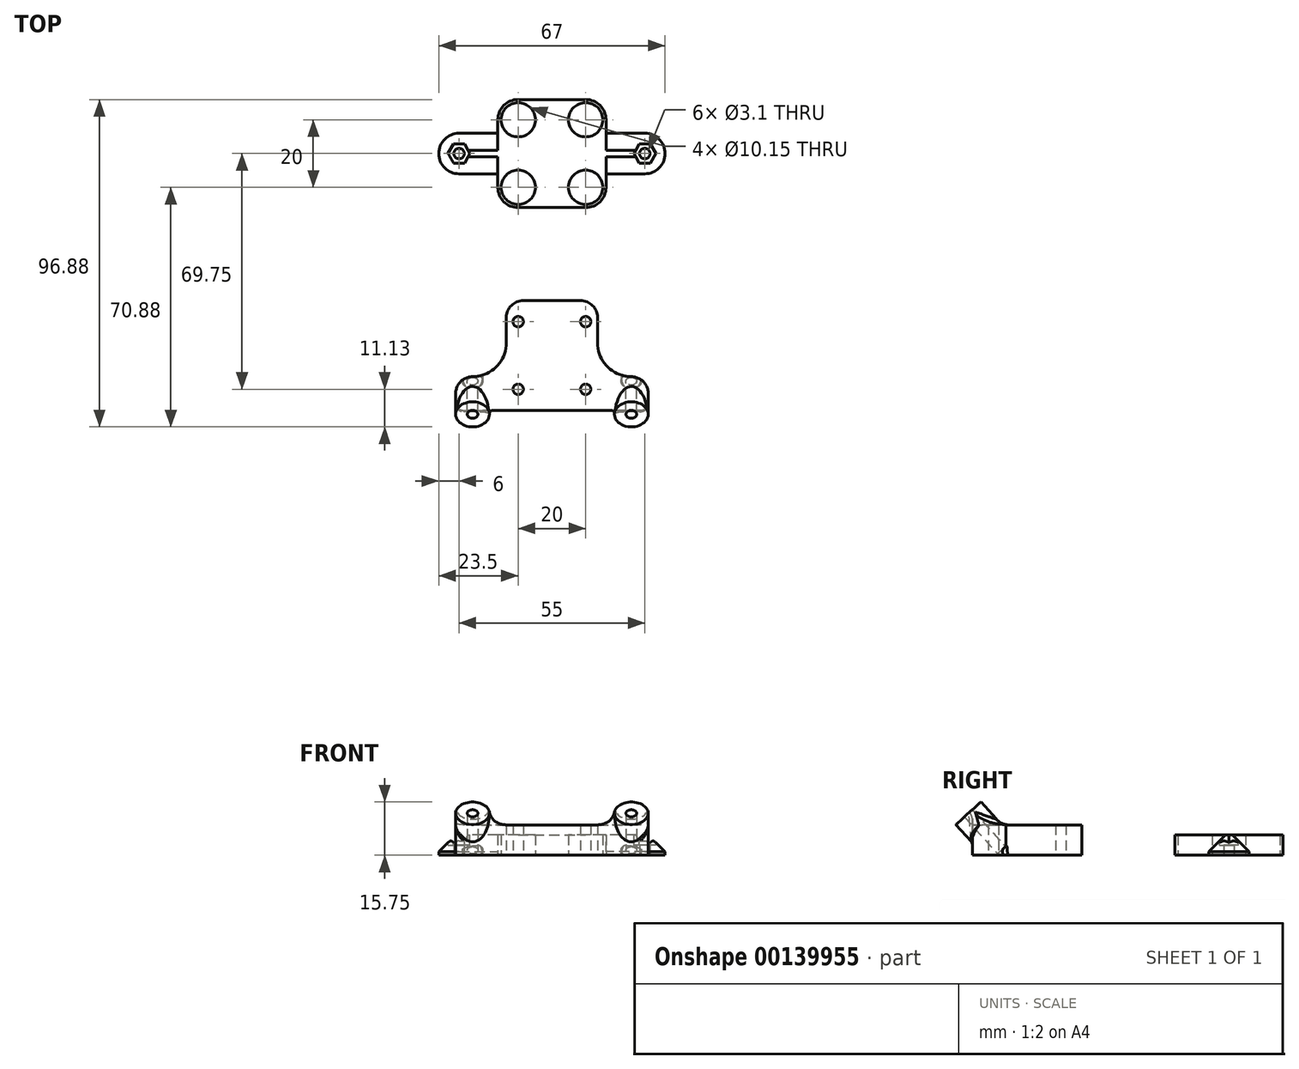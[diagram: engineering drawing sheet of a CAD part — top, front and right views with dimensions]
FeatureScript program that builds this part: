
annotation { "Feature Type Name" : "Feature", "Feature Type Description" : "" }
export const myFeature = defineFeature(function(context is Context, id is Id, definition is map)
    precondition{}
    {
        {
            var Q0;
            Q0=qCreatedBy(makeId("Top.planeOp"),FACE);
            var sketch = newSketch(context, id + "F0", { "sketchPlane" : qUnion([Q0])});
            skLineSegment(sketch, "E0.bottom", {"start": v(-13.5, 22.5) * mm, "end": v(13.5, 22.5) * mm});
            skLineSegment(sketch, "E0.top", {"start": v(-13.5, -10) * mm, "end": v(13.5, -10) * mm});
            skLineSegment(sketch, "E0.left", {"start": v(-13.5, 22.5) * mm, "end": v(-13.5, -10) * mm});
            skLineSegment(sketch, "E0.right", {"start": v(13.5, 22.5) * mm, "end": v(13.5, -10) * mm});
            skLineSegment(sketch, "E1.bottom", {"start": v(-28.5, 0) * mm, "end": v(28.5, 0) * mm});
            skLineSegment(sketch, "E1.top", {"start": v(-28.5, -10) * mm, "end": v(28.5, -10) * mm});
            skLineSegment(sketch, "E1.left", {"start": v(-28.5, 0) * mm, "end": v(-28.5, -10) * mm});
            skLineSegment(sketch, "E1.right", {"start": v(28.5, 0) * mm, "end": v(28.5, -10) * mm});
            skPoint(sketch, "E2", {"position": v(0, 0) * mm});
            skCircle(sketch, "E3", {"center": v(-10, 16.25) * mm, "radius": 1.55 * mm});
            skCircle(sketch, "E4", {"center": v(10, 16.25) * mm, "radius": 1.55 * mm});
            skCircle(sketch, "E5", {"center": v(-10, -3.75) * mm, "radius": 1.55 * mm});
            skCircle(sketch, "E6", {"center": v(10, -3.75) * mm, "radius": 1.55 * mm});
            skLineSegment(sketch, "E7", {"start": v(-10, 16.25) * mm, "end": v(-13.5, 16.25) * mm, "construction": true});
            skLineSegment(sketch, "E8", {"start": v(-10, 16.25) * mm, "end": v(-10, 22.5) * mm, "construction": true});
            skLineSegment(sketch, "E9", {"start": v(10, 16.25) * mm, "end": v(13.5, 16.25) * mm, "construction": true});
            skLineSegment(sketch, "E10", {"start": v(-10, -3.75) * mm, "end": v(-10, -10) * mm, "construction": true});
            skPoint(sketch, "E11", {"position": v(0, -10) * mm});
            skSolve(sketch);
        }
        {
            var Q0;
            {var subQ1=sQuery(id+"F0.wireOp",EDGE,"E0.bottom");Q0=makeQuery(id+"F0.imprint","IMPRINT",FACE,{"disambiguationData":[TD([[makeQuery(id+"F0.imprint","IMPRINT",EDGE,{"derivedFrom":subQ1}),-1.0]])]});}
            var Q1;
            Q1=makeQuery(id+"F0.imprint","IMPRINT",FACE,{"disambiguationData":[TD([[makeQuery(id+"F0.imprint","IMPRINT",EDGE,{"derivedFrom":sQuery(id+"F0.wireOp",EDGE,"E5")}),-1.0]])]});
            var Q2;
            {var subQ5=sQuery(id+"F0.wireOp",EDGE,"E1.right");Q2=makeQuery(id+"F0.imprint","IMPRINT",FACE,{"disambiguationData":[TD([[makeQuery(id+"F0.imprint","IMPRINT",EDGE,{"derivedFrom":subQ5}),-1.0]])]});}
            var Q3;
            {var subQ5=sQuery(id+"F0.wireOp",EDGE,"E1.left");Q3=makeQuery(id+"F0.imprint","IMPRINT",FACE,{"disambiguationData":[TD([[makeQuery(id+"F0.imprint","IMPRINT",EDGE,{"derivedFrom":subQ5}),1.0]])]});}
            extrude(context, id + "F1", {"entities" : qUnion([Q0, Q1, Q2, Q3]), "depth" : 9 * mm, "offsetDistance" : 25 * mm});
        }
        {
            var Q0;
            {var subQ5=sQuery(id+"F0.wireOp",EDGE,"E1.left");Q0=makeQuery(id+"F0.imprint","IMPRINT",FACE,{"disambiguationData":[TD([[makeQuery(id+"F0.imprint","IMPRINT",EDGE,{"derivedFrom":subQ5}),1.0]])]});}
            var Q1;
            {var subQ5=sQuery(id+"F0.wireOp",EDGE,"E1.right");Q1=makeQuery(id+"F0.imprint","IMPRINT",FACE,{"disambiguationData":[TD([[makeQuery(id+"F0.imprint","IMPRINT",EDGE,{"derivedFrom":subQ5}),-1.0]])]});}
            extrude(context, id + "F2", {"entities" : qUnion([Q0, Q1]), "operationType" : NewBodyOperationType.ADD, "depth" : 5 * mm, "offsetDistance" : 25 * mm});
        }
        {
            var Q0;
            Q0=sQuery(id+"F0.wireOp",VERTEX,"E1.top.end");
            var Q1;
            Q1=makeQuery(id+"F1.opExtrude","CAP_VERTEX",VERTEX,{"disambiguationData":[OSD([sQuery(id+"F0.wireOp",EDGE,"E1.bottom"),sQuery(id+"F0.wireOp",EDGE,"E1.right")])],"isStart":false});
            var Q2;
            Q2=sQuery(id+"F0.wireOp",VERTEX,"E1.top.start");
            cPlane(context, id + "F3", {"entities" : qUnion([Q0, Q1, Q2]), "cplaneType" : CPlaneType.THREE_POINT, "offset" : 25 * mm, "width" : 150 * mm, "height" : 150 * mm});
        }
        {
            var Q0;
            Q0=qCreatedBy(id+"F3.planeOp",FACE);
            var sketch = newSketch(context, id + "F4", { "sketchPlane" : qUnion([Q0])});
            skLineSegment(sketch, "E12", {"start": v(-23.5, 0) * mm, "end": v(23.5, 0) * mm, "construction": true});
            skCircle(sketch, "E13", {"center": v(-23.5, 0) * mm, "radius": 5 * mm});
            skCircle(sketch, "E14", {"center": v(23.5, 0) * mm, "radius": 5 * mm});
            skPoint(sketch, "E15", {"position": v(0, 0) * mm});
            skCircle(sketch, "E16", {"center": v(23.5, 0) * mm, "radius": 1.57 * mm});
            skCircle(sketch, "E17", {"center": v(-23.5, 0) * mm, "radius": 1.57 * mm});
            skSolve(sketch);
        }
        {
            var Q0;
            Q0 = qSketchRegion(id + "F4", true);
            extrude(context, id + "F5", {"entities" : qUnion([Q0]), "operationType" : NewBodyOperationType.ADD, "oppositeDirection" : true, "depth" : 10 * mm, "offsetDistance" : 25 * mm});
        }
        {
            var Q0;
            Q0=makeQuery(id+"F1.opExtrude","SWEPT_EDGE",EDGE,{"disambiguationData":[OSD([sQuery(id+"F0.wireOp",EDGE,"E0.bottom"),sQuery(id+"F0.wireOp",EDGE,"E0.left")])]});
            var Q1;
            Q1=makeQuery(id+"F1.opExtrude","SWEPT_EDGE",EDGE,{"disambiguationData":[OSD([sQuery(id+"F0.wireOp",EDGE,"E0.bottom"),sQuery(id+"F0.wireOp",EDGE,"E0.right")])]});
            var Q2;
            Q2=makeQuery(id+"F7.opFillet","BLEND_EDGE",EDGE,{"blendedFrom":[makeQuery(id+"F1.opExtrude","SWEPT_EDGE",EDGE,{"disambiguationData":[OSD([sQuery(id+"F0.wireOp",EDGE,"E0.left"),sQuery(id+"F0.wireOp",EDGE,"E1.bottom")])]}),makeQuery(id+"F1.opExtrude","SWEPT_FACE",FACE,{"disambiguationData":[OSD([sQuery(id+"F0.wireOp",EDGE,"E1.left")])]})],"blendedInto":[makeQuery(id+"F1.opExtrude","SWEPT_FACE",FACE,{"disambiguationData":[OSD([sQuery(id+"F0.wireOp",EDGE,"E1.left")])]})]});
            var Q3;
            Q3=makeQuery(id+"F7.opFillet","BLEND_EDGE",EDGE,{"blendedFrom":[makeQuery(id+"F1.opExtrude","SWEPT_EDGE",EDGE,{"disambiguationData":[OSD([sQuery(id+"F0.wireOp",EDGE,"E0.right"),sQuery(id+"F0.wireOp",EDGE,"E1.bottom")])]}),makeQuery(id+"F1.opExtrude","SWEPT_FACE",FACE,{"disambiguationData":[OSD([sQuery(id+"F0.wireOp",EDGE,"E1.right")])]})],"blendedInto":[makeQuery(id+"F1.opExtrude","SWEPT_FACE",FACE,{"disambiguationData":[OSD([sQuery(id+"F0.wireOp",EDGE,"E1.right")])]})]});
            var Q4;
            Q4=makeQuery(id+"F1.opExtrude","SWEPT_EDGE",EDGE,{"disambiguationData":[OSD([sQuery(id+"F0.wireOp",EDGE,"E1.bottom"),sQuery(id+"F0.wireOp",EDGE,"E1.left")])]});
            var Q5;
            Q5=makeQuery(id+"F1.opExtrude","SWEPT_EDGE",EDGE,{"disambiguationData":[OSD([sQuery(id+"F0.wireOp",EDGE,"E1.bottom"),sQuery(id+"F0.wireOp",EDGE,"E1.right")])]});
            fillet(context, id + "F6", {"entities" : qUnion([Q0, Q1, Q2, Q3, Q4, Q5]), "radius" : 5 * mm, "tangentPropagation" : true, "allowEdgeOverflow" : false});
        }
        {
            var Q0;
            Q0=makeQuery(id+"F1.opExtrude","SWEPT_EDGE",EDGE,{"disambiguationData":[OSD([sQuery(id+"F0.wireOp",EDGE,"E0.left"),sQuery(id+"F0.wireOp",EDGE,"E1.bottom")])]});
            var Q1;
            Q1=makeQuery(id+"F1.opExtrude","SWEPT_EDGE",EDGE,{"disambiguationData":[OSD([sQuery(id+"F0.wireOp",EDGE,"E0.right"),sQuery(id+"F0.wireOp",EDGE,"E1.bottom")])]});
            fillet(context, id + "F7", {"entities" : qUnion([Q0, Q1]), "radius" : 10 * mm, "tangentPropagation" : true, "allowEdgeOverflow" : false});
        }
        {
            var Q0;
            Q0=makeQuery(id+"F1.opExtrude","SWEPT_EDGE",EDGE,{"disambiguationData":[OSD([sQuery(id+"F0.wireOp",EDGE,"E1.top"),sQuery(id+"F0.wireOp",EDGE,"E1.left")])]});
            var Q1;
            Q1=makeQuery(id+"F1.opExtrude","SWEPT_EDGE",EDGE,{"disambiguationData":[OSD([sQuery(id+"F0.wireOp",EDGE,"E1.top"),sQuery(id+"F0.wireOp",EDGE,"E1.right")])]});
            fillet(context, id + "F8", {"entities" : qUnion([Q0, Q1]), "radius" : 2 * mm, "tangentPropagation" : true, "allowEdgeOverflow" : false});
        }
        {
            var Q0;
            Q0=makeQuery(id+"F5.boolean.opBoolean","INTERSECT",EDGE,{"disambiguationData":[OD(1.0)],"derivedFrom":[makeQuery(id+"F1.opExtrude","CAP_FACE",FACE,{"disambiguationData":[OSD([sQuery(id+"F0.wireOp",EDGE,"E0.bottom"),sQuery(id+"F0.wireOp",EDGE,"E0.left"),sQuery(id+"F0.wireOp",EDGE,"E0.right"),sQuery(id+"F0.wireOp",EDGE,"E1.bottom"),sQuery(id+"F0.wireOp",EDGE,"E1.top"),sQuery(id+"F0.wireOp",EDGE,"E1.left"),sQuery(id+"F0.wireOp",EDGE,"E1.right"),sQuery(id+"F0.wireOp",EDGE,"E3"),sQuery(id+"F0.wireOp",EDGE,"E4"),sQuery(id+"F0.wireOp",EDGE,"E5"),sQuery(id+"F0.wireOp",EDGE,"E6")])],"isStart":false}),makeQuery(id+"F5.opExtrude","SWEPT_FACE",FACE,{"disambiguationData":[OSD([sQuery(id+"F4.wireOp",EDGE,"E14")])]})]});
            var Q1;
            Q1=makeQuery(id+"F5.boolean.opBoolean","INTERSECT",EDGE,{"disambiguationData":[OD(1.0)],"derivedFrom":[makeQuery(id+"F1.opExtrude","CAP_FACE",FACE,{"disambiguationData":[OSD([sQuery(id+"F0.wireOp",EDGE,"E0.bottom"),sQuery(id+"F0.wireOp",EDGE,"E0.left"),sQuery(id+"F0.wireOp",EDGE,"E0.right"),sQuery(id+"F0.wireOp",EDGE,"E1.bottom"),sQuery(id+"F0.wireOp",EDGE,"E1.top"),sQuery(id+"F0.wireOp",EDGE,"E1.left"),sQuery(id+"F0.wireOp",EDGE,"E1.right"),sQuery(id+"F0.wireOp",EDGE,"E3"),sQuery(id+"F0.wireOp",EDGE,"E4"),sQuery(id+"F0.wireOp",EDGE,"E5"),sQuery(id+"F0.wireOp",EDGE,"E6")])],"isStart":false}),makeQuery(id+"F5.opExtrude","SWEPT_FACE",FACE,{"disambiguationData":[OSD([sQuery(id+"F4.wireOp",EDGE,"E13")])]})]});
            fillet(context, id + "F9", {"entities" : qUnion([Q0, Q1]), "radius" : 5 * mm, "tangentPropagation" : true, "allowEdgeOverflow" : false});
        }
        {
            var Q0;
            Q0=makeQuery(id+"F5.boolean.opBoolean","INTERSECT",EDGE,{"derivedFrom":[makeQuery(id+"F1.opExtrude","SWEPT_FACE",FACE,{"disambiguationData":[OSD([sQuery(id+"F0.wireOp",EDGE,"E1.top")])]}),makeQuery(id+"F5.opExtrude","SWEPT_FACE",FACE,{"disambiguationData":[OSD([sQuery(id+"F4.wireOp",EDGE,"E14")])]})]});
            var Q1;
            Q1=makeQuery(id+"F5.boolean.opBoolean","INTERSECT",EDGE,{"derivedFrom":[makeQuery(id+"F1.opExtrude","SWEPT_FACE",FACE,{"disambiguationData":[OSD([sQuery(id+"F0.wireOp",EDGE,"E1.top")])]}),makeQuery(id+"F5.opExtrude","SWEPT_FACE",FACE,{"disambiguationData":[OSD([sQuery(id+"F4.wireOp",EDGE,"E13")])]})]});
            fillet(context, id + "F10", {"entities" : qUnion([Q0, Q1]), "radius" : 1 * mm, "tangentPropagation" : true, "allowEdgeOverflow" : false});
        }
        {
            var Q0;
            Q0=makeQuery(id+"F4.imprint","IMPRINT",FACE,{"disambiguationData":[TD([[makeQuery(id+"F4.imprint","IMPRINT",EDGE,{"derivedFrom":sQuery(id+"F4.wireOp",EDGE,"E16")}),1.0]])]});
            var Q1;
            Q1=makeQuery(id+"F4.imprint","IMPRINT",FACE,{"disambiguationData":[TD([[makeQuery(id+"F4.imprint","IMPRINT",EDGE,{"derivedFrom":sQuery(id+"F4.wireOp",EDGE,"E17")}),1.0]])]});
            var Q2;
            Q2=sQuery(id+"F4.wireOp",EDGE,"E17");
            var Q3;
            Q3=sQuery(id+"F4.wireOp",EDGE,"E16");
            extrude(context, id + "F11", {"entities" : qUnion([Q0, Q1]), "operationType" : NewBodyOperationType.REMOVE, "surfaceEntities" : qUnion([Q2, Q3]), "depth" : 25 * mm, "offsetDistance" : 25 * mm, "symmetric" : true});
        }
        {
            var Q0;
            Q0=sQuery(id+"F0.wireOp",EDGE,"E1.bottom");
            cPoint(context, id + "F12", {"entities" : qUnion([Q0]), "parameter" : 0.5});
        }
        {
            var Q0;
            Q0 = qCreatedBy(id + "F12" ,VERTEX);
            var Q1;
            Q1=qCreatedBy(id+"F3.planeOp",FACE);
            cPlane(context, id + "F13", {"entities" : qUnion([Q0, Q1]), "cplaneType" : CPlaneType.PLANE_POINT, "offset" : 25 * mm, "width" : 150 * mm, "height" : 150 * mm});
        }
        {
            var Q0;
            Q0=qCreatedBy(id+"F13.planeOp",FACE);
            var sketch = newSketch(context, id + "F14", { "sketchPlane" : qUnion([Q0])});
            skCircle(sketch, "E18", {"center": v(-23.5, 0) * mm, "radius": 3 * mm});
            skCircle(sketch, "E19", {"center": v(23.5, 0) * mm, "radius": 3 * mm});
            skSolve(sketch);
        }
        {
            var Q0;
            Q0 = qSketchRegion(id + "F14", true);
            extrude(context, id + "F15", {"entities" : qUnion([Q0]), "operationType" : NewBodyOperationType.REMOVE, "depth" : 4 * mm, "offsetDistance" : 25 * mm, "symmetric" : true});
        }
        {
            var Q0;
            Q0=qCreatedBy(makeId("Top.planeOp"),FACE);
            var sketch = newSketch(context, id + "F16", { "sketchPlane" : qUnion([Q0])});
            skLineSegment(sketch, "E20.bottom", {"start": v(-10, 82) * mm, "end": v(10, 82) * mm});
            skLineSegment(sketch, "E20.top", {"start": v(-10, 50) * mm, "end": v(10, 50) * mm});
            skPoint(sketch, "E21", {"position": v(0, 82) * mm});
            skCircle(sketch, "E22", {"center": v(-10, 76) * mm, "radius": 5.08 * mm});
            skCircle(sketch, "E23", {"center": v(-10, 56) * mm, "radius": 5.08 * mm});
            skCircle(sketch, "E24", {"center": v(10, 76) * mm, "radius": 5.08 * mm});
            skCircle(sketch, "E25", {"center": v(10, 56) * mm, "radius": 5.08 * mm});
            skLineSegment(sketch, "E26.bottom", {"start": v(-10, 76) * mm, "end": v(10, 76) * mm, "construction": true});
            skLineSegment(sketch, "E26.top", {"start": v(-10, 56) * mm, "end": v(10, 56) * mm, "construction": true});
            skLineSegment(sketch, "E26.left", {"start": v(-10, 76) * mm, "end": v(-10, 56) * mm, "construction": true});
            skLineSegment(sketch, "E26.right", {"start": v(10, 76) * mm, "end": v(10, 56) * mm, "construction": true});
            skPoint(sketch, "E27", {"position": v(0, 76) * mm});
            skPoint(sketch, "E28", {"position": v(10, 66) * mm});
            skPoint(sketch, "E29", {"position": v(33.5, 66) * mm});
            skCircle(sketch, "E30", {"center": v(-27.5, 66) * mm, "radius": 1.55 * mm});
            skCircle(sketch, "E31", {"center": v(27.5, 66) * mm, "radius": 1.55 * mm});
            skArc(sketch, "E32", {"start": v(-27.5, 72) * mm, "mid": v(-33.5, 66) * mm, "end": v(-27.5, 60) * mm});
            skArc(sketch, "E33", {"start": v(27.5, 60) * mm, "mid": v(33.5, 66) * mm, "end": v(27.5, 72) * mm});
            skArc(sketch, "E34", {"start": v(-10, 82) * mm, "mid": v(-14.24, 80.24) * mm, "end": v(-16, 76) * mm});
            skArc(sketch, "E35", {"start": v(16, 76) * mm, "mid": v(14.24, 80.24) * mm, "end": v(10, 82) * mm});
            skArc(sketch, "E36", {"start": v(10, 50) * mm, "mid": v(14.24, 51.76) * mm, "end": v(16, 56) * mm});
            skArc(sketch, "E37", {"start": v(-16, 56) * mm, "mid": v(-14.24, 51.76) * mm, "end": v(-10, 50) * mm});
            skLineSegment(sketch, "E38", {"start": v(-27.5, 72) * mm, "end": v(-16, 72) * mm});
            skLineSegment(sketch, "E39", {"start": v(-16, 72) * mm, "end": v(-16, 76) * mm});
            skLineSegment(sketch, "E40", {"start": v(-27.5, 60) * mm, "end": v(-16, 60) * mm});
            skLineSegment(sketch, "E41", {"start": v(-16, 60) * mm, "end": v(-16, 56) * mm});
            skLineSegment(sketch, "E42", {"start": v(16, 76) * mm, "end": v(16, 72) * mm});
            skLineSegment(sketch, "E43", {"start": v(16, 72) * mm, "end": v(27.5, 72) * mm});
            skLineSegment(sketch, "E44", {"start": v(16, 56) * mm, "end": v(16, 60) * mm});
            skLineSegment(sketch, "E45", {"start": v(16, 60) * mm, "end": v(27.5, 60) * mm});
            skPoint(sketch, "E46", {"position": v(-33.5, 66) * mm});
            skSolve(sketch);
        }
        {
            var Q0;
            Q0=makeQuery(id+"F16.imprint","IMPRINT",FACE,{"disambiguationData":[TD([[makeQuery(id+"F16.imprint","IMPRINT",EDGE,{"derivedFrom":sQuery(id+"F16.wireOp",EDGE,"E20.bottom")}),-1.0]])]});
            extrude(context, id + "F17", {"entities" : qUnion([Q0]), "depth" : 6 * mm, "offsetDistance" : 25 * mm});
        }
        {
            var Q0;
            Q0=makeQuery(id+"F17.opExtrude","CAP_FACE",FACE,{"disambiguationData":[OSD([sQuery(id+"F16.wireOp",EDGE,"E20.bottom"),sQuery(id+"F16.wireOp",EDGE,"E20.top"),sQuery(id+"F16.wireOp",EDGE,"E22"),sQuery(id+"F16.wireOp",EDGE,"E23"),sQuery(id+"F16.wireOp",EDGE,"E24"),sQuery(id+"F16.wireOp",EDGE,"E25"),sQuery(id+"F16.wireOp",EDGE,"E30"),sQuery(id+"F16.wireOp",EDGE,"E31"),sQuery(id+"F16.wireOp",EDGE,"E32"),sQuery(id+"F16.wireOp",EDGE,"E33"),sQuery(id+"F16.wireOp",EDGE,"E34"),sQuery(id+"F16.wireOp",EDGE,"E35"),sQuery(id+"F16.wireOp",EDGE,"E36"),sQuery(id+"F16.wireOp",EDGE,"E37"),sQuery(id+"F16.wireOp",EDGE,"E38"),sQuery(id+"F16.wireOp",EDGE,"E39"),sQuery(id+"F16.wireOp",EDGE,"E40"),sQuery(id+"F16.wireOp",EDGE,"E41"),sQuery(id+"F16.wireOp",EDGE,"E42"),sQuery(id+"F16.wireOp",EDGE,"E43"),sQuery(id+"F16.wireOp",EDGE,"E44"),sQuery(id+"F16.wireOp",EDGE,"E45")])],"isStart":false});
            var sketch = newSketch(context, id + "F18", { "sketchPlane" : qUnion([Q0])});
            skCircle(sketch, "E47.cCircle", {"center": v(-27.5, 66) * mm, "radius": 2.8 * mm, "construction": true});
            skLineSegment(sketch, "E47.0", {"start": v(-24.27, 66) * mm, "end": v(-25.88, 63.2) * mm});
            skLineSegment(sketch, "E47.1", {"start": v(-25.88, 63.2) * mm, "end": v(-29.12, 63.2) * mm});
            skLineSegment(sketch, "E47.2", {"start": v(-29.12, 63.2) * mm, "end": v(-30.73, 66) * mm});
            skLineSegment(sketch, "E47.3", {"start": v(-30.73, 66) * mm, "end": v(-29.12, 68.8) * mm});
            skLineSegment(sketch, "E47.4", {"start": v(-29.12, 68.8) * mm, "end": v(-25.88, 68.8) * mm});
            skLineSegment(sketch, "E47.5", {"start": v(-25.88, 68.8) * mm, "end": v(-24.27, 66) * mm});
            skPoint(sketch, "E47.0.midPoint", {"position": v(-25.08, 64.6) * mm});
            skCircle(sketch, "E48.cCircle", {"center": v(27.5, 66) * mm, "radius": 2.8 * mm, "construction": true});
            skLineSegment(sketch, "E48.0", {"start": v(25.88, 63.2) * mm, "end": v(24.27, 66) * mm});
            skLineSegment(sketch, "E48.1", {"start": v(24.27, 66) * mm, "end": v(25.88, 68.8) * mm});
            skLineSegment(sketch, "E48.2", {"start": v(25.88, 68.8) * mm, "end": v(29.12, 68.8) * mm});
            skLineSegment(sketch, "E48.3", {"start": v(29.12, 68.8) * mm, "end": v(30.73, 66) * mm});
            skLineSegment(sketch, "E48.4", {"start": v(30.73, 66) * mm, "end": v(29.12, 63.2) * mm});
            skLineSegment(sketch, "E48.5", {"start": v(29.12, 63.2) * mm, "end": v(25.88, 63.2) * mm});
            skPoint(sketch, "E48.0.midPoint", {"position": v(25.08, 64.6) * mm});
            skSolve(sketch);
        }
        {
            var Q0;
            Q0 = qSketchRegion(id + "F18", true);
            extrude(context, id + "F19", {"entities" : qUnion([Q0]), "operationType" : NewBodyOperationType.REMOVE, "oppositeDirection" : true, "depth" : 3 * mm, "offsetDistance" : 25 * mm});
        }
        {
            var Q0;
            Q0=makeQuery(id+"F17.opExtrude","CAP_EDGE",EDGE,{"disambiguationData":[OSD([sQuery(id+"F16.wireOp",EDGE,"E32")])],"isStart":false});
            var Q1;
            Q1=makeQuery(id+"F17.opExtrude","CAP_EDGE",EDGE,{"disambiguationData":[OSD([sQuery(id+"F16.wireOp",EDGE,"E38")])],"isStart":false});
            var Q2;
            Q2=makeQuery(id+"F17.opExtrude","CAP_EDGE",EDGE,{"disambiguationData":[OSD([sQuery(id+"F16.wireOp",EDGE,"E40")])],"isStart":false});
            var Q3;
            Q3=makeQuery(id+"F17.opExtrude","CAP_EDGE",EDGE,{"disambiguationData":[OSD([sQuery(id+"F16.wireOp",EDGE,"E45")])],"isStart":false});
            var Q4;
            Q4=makeQuery(id+"F17.opExtrude","CAP_EDGE",EDGE,{"disambiguationData":[OSD([sQuery(id+"F16.wireOp",EDGE,"E33")])],"isStart":false});
            var Q5;
            Q5=makeQuery(id+"F17.opExtrude","CAP_EDGE",EDGE,{"disambiguationData":[OSD([sQuery(id+"F16.wireOp",EDGE,"E43")])],"isStart":false});
            chamfer(context, id + "F20", {"entities" : qUnion([Q0, Q1, Q2, Q3, Q4, Q5]), "width" : 5 * mm, "tangentPropagation" : true});
        }
    });
